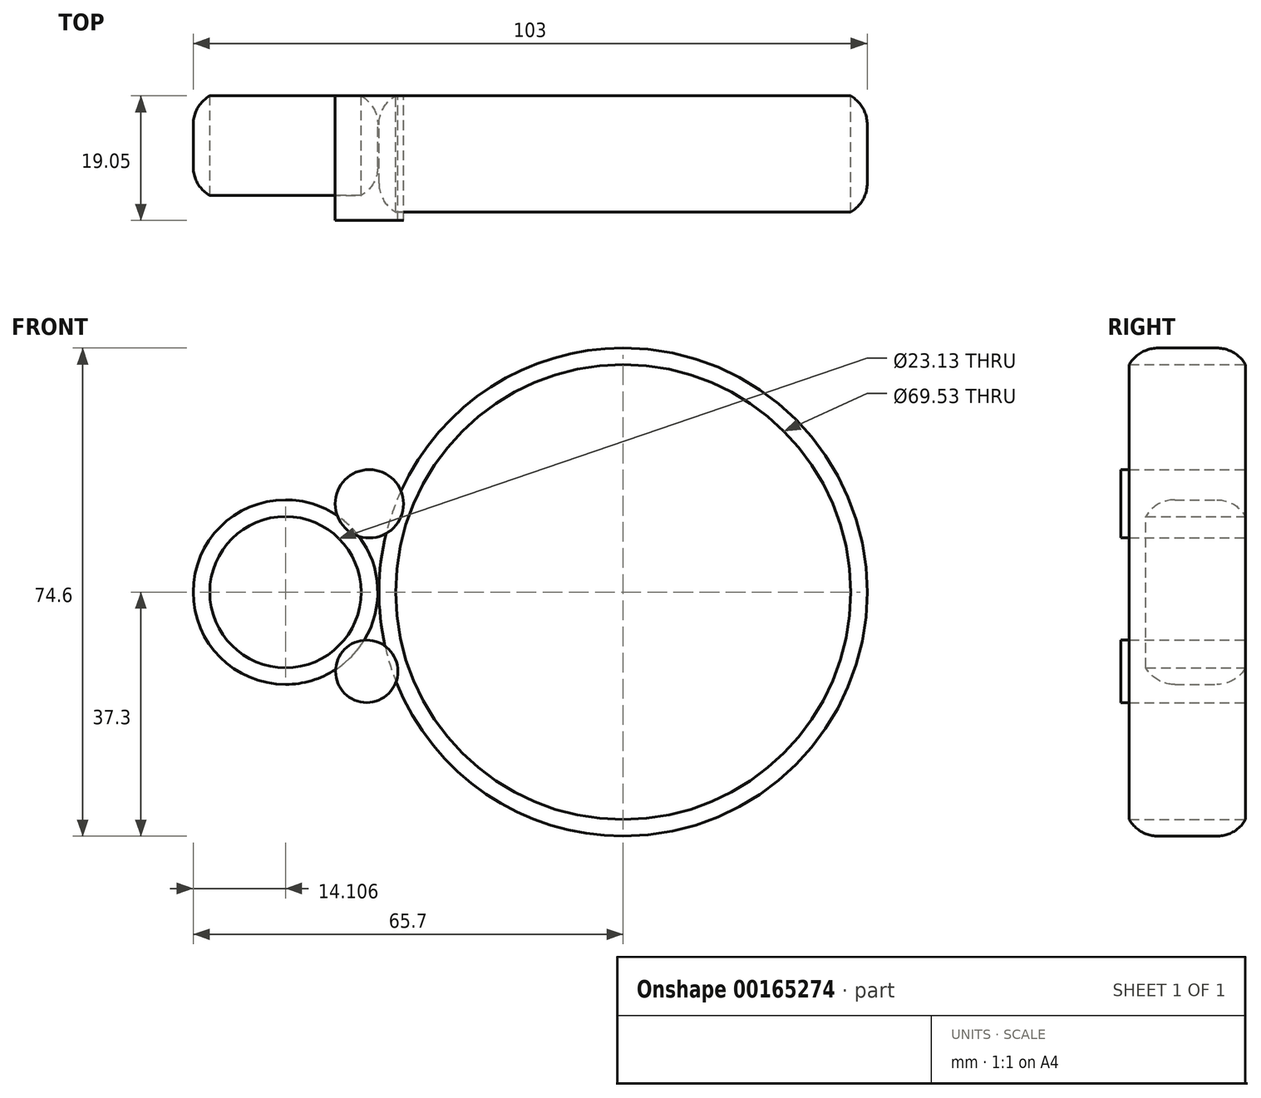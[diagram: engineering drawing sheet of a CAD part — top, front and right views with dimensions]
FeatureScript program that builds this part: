
annotation { "Feature Type Name" : "Feature", "Feature Type Description" : "" }
export const myFeature = defineFeature(function(context is Context, id is Id, definition is map)
    precondition{}
    {
        {
            var Q0;
            Q0=qCreatedBy(makeId("Front.planeOp"),FACE);
            var sketch = newSketch(context, id + "F0", { "sketchPlane" : qUnion([Q0])});
            skCircle(sketch, "E0", {"center": v(0, 0) * mm, "radius": 37.3 * mm});
            skSolve(sketch);
        }
        {
            var Q0;
            Q0=makeQuery(id+"F0.imprint","IMPRINT",FACE,{"disambiguationData":[TD([[makeQuery(id+"F0.imprint","IMPRINT",EDGE,{"derivedFrom":sQuery(id+"F0.wireOp",EDGE,"E0")}),1.0]])]});
            extrude(context, id + "F1", {"entities" : qUnion([Q0]), "depth" : 17.78 * mm});
        }
        {
            var Q0;
            Q0=qCreatedBy(makeId("Front.planeOp"),FACE);
            var sketch = newSketch(context, id + "F2", { "sketchPlane" : qUnion([Q0])});
            skCircle(sketch, "E1", {"center": v(-51.6, 0) * mm, "radius": 14.1 * mm});
            skLineSegment(sketch, "E2", {"start": v(-42.06, 10.4) * mm, "end": v(-34.58, 14.62) * mm});
            skLineSegment(sketch, "E3", {"start": v(-42.12, -10.45) * mm, "end": v(-34.34, -14.7) * mm});
            skSolve(sketch);
        }
        {
            var Q0;
            {var subQ0=sQuery(id+"F2.wireOp",EDGE,"E1");var subQ1=makeQuery(id+"F2.imprint","IMPRINT",VERTEX,{"disambiguationData":[OD(0.0)],"derivedFrom":subQ0});Q0=makeQuery(id+"F2.imprint","IMPRINT",FACE,{"disambiguationData":[TD([[makeQuery(id+"F2.imprint","IMPRINT",EDGE,{"disambiguationData":[TD([[subQ1,-1.0]])],"derivedFrom":subQ0}),1.0]])]});}
            extrude(context, id + "F3", {"entities" : qUnion([Q0]), "depth" : 15.24 * mm});
        }
        {
            var Q0;
            Q0=makeQuery(id+"F3.opExtrude","CAP_FACE",FACE,{"disambiguationData":[OSD([sQuery(id+"F2.wireOp",EDGE,"E1")])],"isStart":false});
            var Q1;
            Q1=makeQuery(id+"F3.opExtrude","CAP_FACE",FACE,{"disambiguationData":[OSD([sQuery(id+"F2.wireOp",EDGE,"E1")])],"isStart":true});
            shell(context, id + "F4", {"entities" : qUnion([Q0, Q1]), "thickness" : 2.54 * mm});
        }
        {
            var Q0;
            Q0=makeQuery(id+"F3.opExtrude","CAP_EDGE",EDGE,{"disambiguationData":[OSD([sQuery(id+"F2.wireOp",EDGE,"E1")])],"isStart":true});
            var Q1;
            Q1=makeQuery(id+"F3.opExtrude","CAP_EDGE",EDGE,{"disambiguationData":[OSD([sQuery(id+"F2.wireOp",EDGE,"E1")])],"isStart":false});
            fillet(context, id + "F5", {"entities" : qUnion([Q0, Q1]), "radius" : 5.08 * mm, "tangentPropagation" : true, "allowEdgeOverflow" : false});
        }
        {
            var Q0;
            Q0=qCreatedBy(makeId("Front.planeOp"),FACE);
            var sketch = newSketch(context, id + "F6", { "sketchPlane" : qUnion([Q0])});
            skCircle(sketch, "E4", {"center": v(-38.78, 13.5) * mm, "radius": 5.22 * mm});
            skCircle(sketch, "E5", {"center": v(-39.18, -12.11) * mm, "radius": 4.76 * mm});
            skSolve(sketch);
        }
        {
            var Q0;
            Q0=makeQuery(id+"F6.imprint","IMPRINT",FACE,{"disambiguationData":[TD([[makeQuery(id+"F6.imprint","IMPRINT",EDGE,{"derivedFrom":sQuery(id+"F6.wireOp",EDGE,"E4")}),1.0]])]});
            var Q1;
            Q1=makeQuery(id+"F6.imprint","IMPRINT",FACE,{"disambiguationData":[TD([[makeQuery(id+"F6.imprint","IMPRINT",EDGE,{"derivedFrom":sQuery(id+"F6.wireOp",EDGE,"E5")}),1.0]])]});
            extrude(context, id + "F7", {"entities" : qUnion([Q0, Q1]), "depth" : 19.05 * mm});
        }
        {
            var Q0;
            Q0=makeQuery(id+"F1.opExtrude","CAP_FACE",FACE,{"disambiguationData":[OSD([sQuery(id+"F0.wireOp",EDGE,"E0")])],"isStart":false});
            var Q1;
            Q1=makeQuery(id+"F1.opExtrude","CAP_FACE",FACE,{"disambiguationData":[OSD([sQuery(id+"F0.wireOp",EDGE,"E0")])],"isStart":true});
            shell(context, id + "F8", {"entities" : qUnion([Q0, Q1]), "thickness" : 2.54 * mm});
        }
        {
            var Q0;
            Q0=makeQuery(id+"F1.opExtrude","CAP_EDGE",EDGE,{"disambiguationData":[OSD([sQuery(id+"F0.wireOp",EDGE,"E0")])],"isStart":true});
            var Q1;
            Q1=makeQuery(id+"F1.opExtrude","CAP_EDGE",EDGE,{"disambiguationData":[OSD([sQuery(id+"F0.wireOp",EDGE,"E0")])],"isStart":false});
            fillet(context, id + "F9", {"entities" : qUnion([Q0, Q1]), "radius" : 5.08 * mm, "tangentPropagation" : true, "allowEdgeOverflow" : false});
        }
    });
